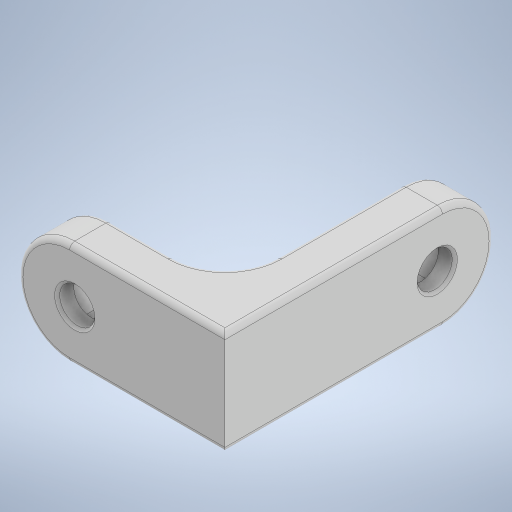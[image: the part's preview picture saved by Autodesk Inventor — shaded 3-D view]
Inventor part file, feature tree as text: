
AUTODESK INVENTOR PART (.ipt)
format: ipt  version: 2024.2 (Build 282272000, 272)  size: 322,048 bytes
history: native  units: mm
features: extrude x6, fillet x3, chamfer x1, projected_geometry x1
ambient origin geometry x8: Origin, YZ Plane, XZ Plane, XY Plane, X Axis, Y Axis, Z Axis, Center Point
bodies: Solid1 (feature_tree)
feature tree (11):
  extrude  "Extrusion1"  Depth=10.0mm
  extrude  "Extrusion2"  Depth=26.0mm
  extrude  "Extrusion3"  Depth=4.0mm TaperAngle=0.0deg
  extrude  "Extrusion4"  Depth=20.0mm
  extrude  "Extrusion5"  Depth=4.0mm TaperAngle=0.0deg
  extrude  "Extrusion6"  Depth=5.7mm
  fillet  "Fillet1"  Radius=5.5mm
  fillet  "Fillet2"  Radius=2.4mm
  fillet  "Fillet3"  Radius=3.4mm
  chamfer  "Chamfer1"  Distance=2.4mm
  projected_geometry  "Projected Loop1"
